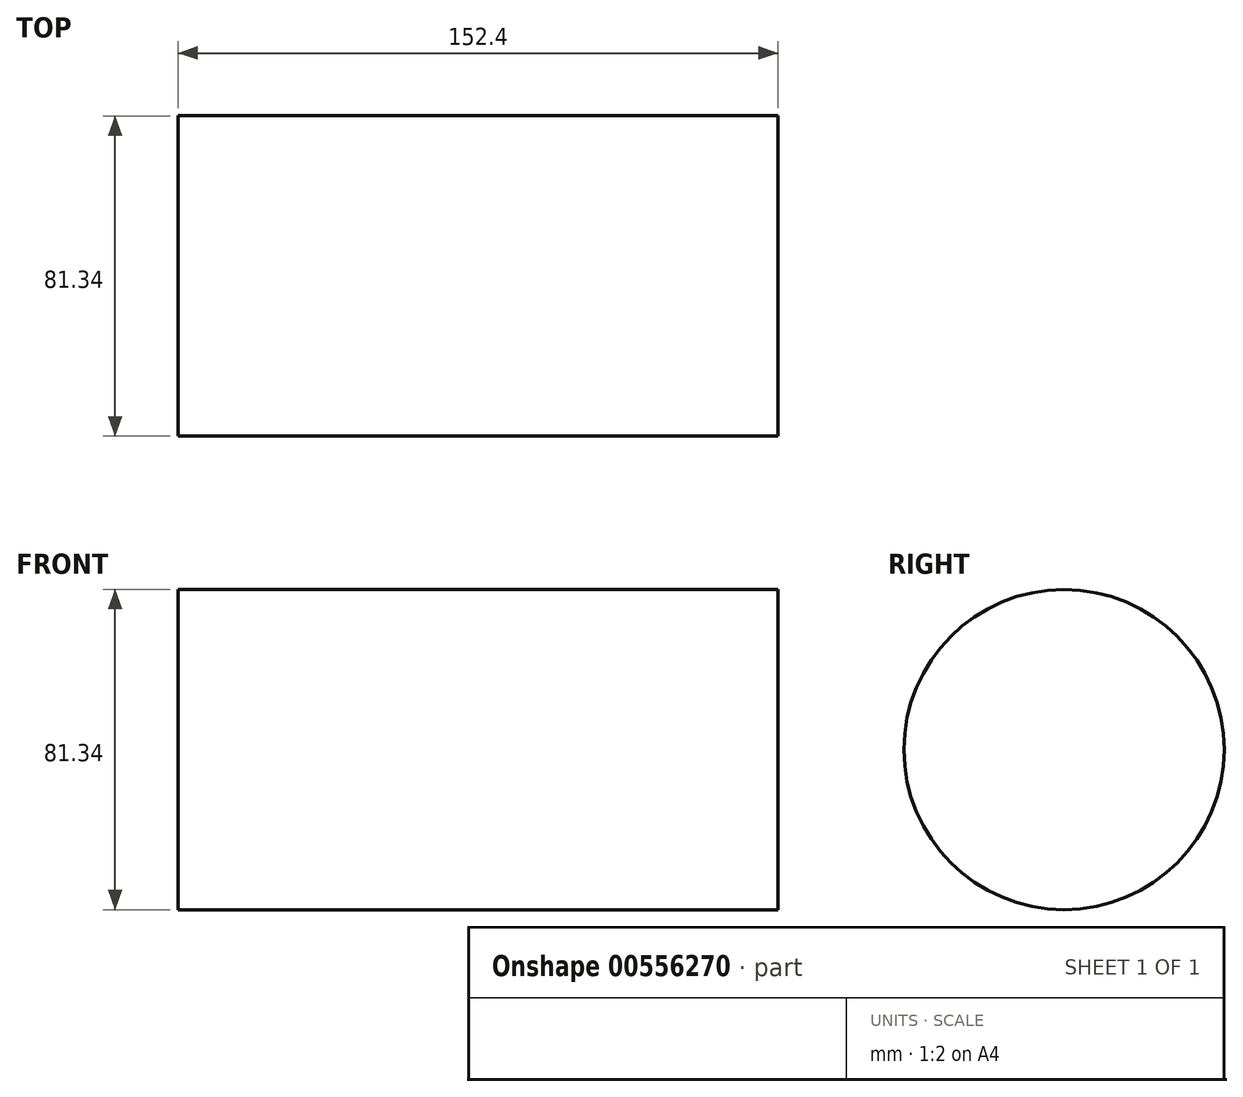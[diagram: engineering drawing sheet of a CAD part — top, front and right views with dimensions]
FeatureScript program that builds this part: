
annotation { "Feature Type Name" : "Feature", "Feature Type Description" : "" }
export const myFeature = defineFeature(function(context is Context, id is Id, definition is map)
    precondition{}
    {
        {
            var Q0;
            Q0=qCreatedBy(makeId("Right.planeOp"),FACE);
            var sketch = newSketch(context, id + "F0", { "sketchPlane" : qUnion([Q0])});
            skCircle(sketch, "E0", {"center": v(0, 0) * mm, "radius": 40.67 * mm});
            skSolve(sketch);
        }
        {
            var Q0;
            Q0=makeQuery(id+"F0.imprint","IMPRINT",FACE,{"disambiguationData":[TD([[makeQuery(id+"F0.imprint","IMPRINT",EDGE,{"derivedFrom":sQuery(id+"F0.wireOp",EDGE,"E0")}),1.0]])]});
            extrude(context, id + "F1", {"entities" : qUnion([Q0]), "depth" : 152.4 * mm, "offsetDistance" : 25.4 * mm});
        }
    });
